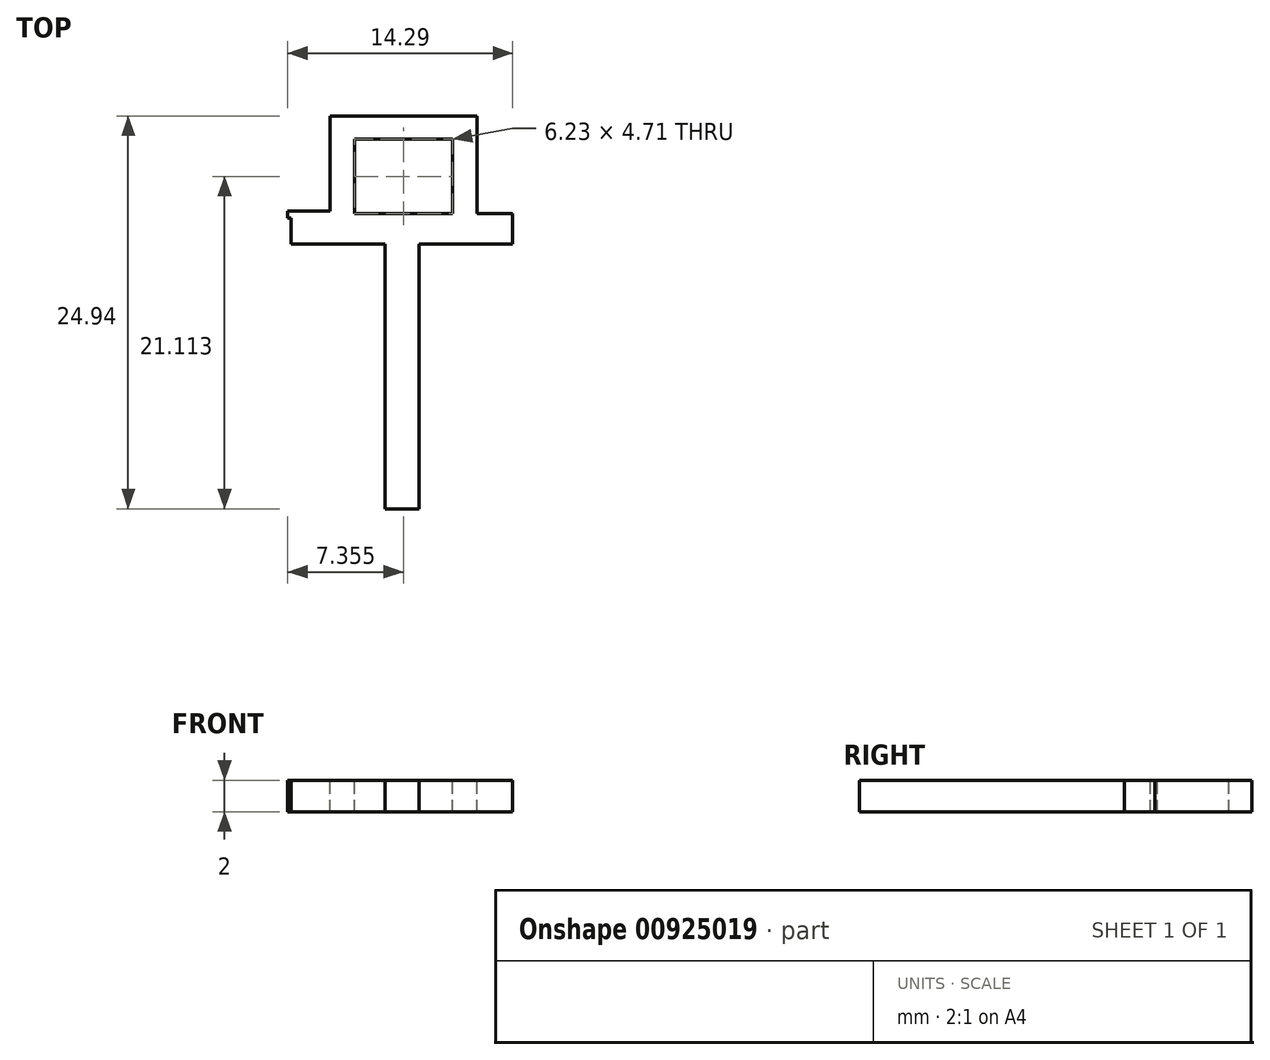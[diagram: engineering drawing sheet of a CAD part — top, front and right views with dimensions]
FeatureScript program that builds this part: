
annotation { "Feature Type Name" : "Feature", "Feature Type Description" : "" }
export const myFeature = defineFeature(function(context is Context, id is Id, definition is map)
    precondition{}
    {
        {
            var Q0;
            Q0=qCreatedBy(makeId("Top.planeOp"),FACE);
            var sketch = newSketch(context, id + "F0", { "sketchPlane" : qUnion([Q0])});
            skText(sketch, "E0", { "text": "T", "fontName": "OpenSans-Regular.ttf"});
            skLineSegment(sketch, "E1", {"start": v(0, 0) * mm, "end": v(16, 0) * mm});
            skLineSegment(sketch, "E2", {"start": v(0, -0.45) * mm, "end": v(0, 0) * mm});
            skLineSegment(sketch, "E3", {"start": v(0, -0.45) * mm, "end": v(16, -0.45) * mm});
            skLineSegment(sketch, "E4", {"start": v(8, -0.45) * mm, "end": v(8, 0) * mm});
            skLineSegment(sketch, "E5.bottom", {"start": v(2.69, -1.92) * mm, "end": v(12.02, -1.92) * mm});
            skLineSegment(sketch, "E5.top", {"start": v(2.69, 6.02) * mm, "end": v(12.02, 6.02) * mm});
            skLineSegment(sketch, "E5.left", {"start": v(2.69, -1.92) * mm, "end": v(2.69, 6.02) * mm});
            skLineSegment(sketch, "E5.right", {"start": v(12.02, -1.92) * mm, "end": v(12.02, 6.02) * mm});
            skLineSegment(sketch, "E6", {"start": v(7.36, 6.02) * mm, "end": v(7.36, -1.92) * mm});
            skLineSegment(sketch, "E7.bottom", {"start": v(10.47, -0.45) * mm, "end": v(4.24, -0.45) * mm});
            skLineSegment(sketch, "E7.top", {"start": v(10.47, 4.55) * mm, "end": v(4.24, 4.55) * mm});
            skLineSegment(sketch, "E7.left", {"start": v(10.47, -0.45) * mm, "end": v(10.47, 4.55) * mm});
            skLineSegment(sketch, "E7.right", {"start": v(4.24, -0.45) * mm, "end": v(4.24, 4.55) * mm});
            skPoint(sketch, "E7.middle", {"position": v(7.36, 2.05) * mm});
            const initialGuessF0  = {"E0": [0, -0.01892, 1, 0, 0.01892]};
            skSetInitialGuess(sketch, initialGuessF0);
            skSolve(sketch);
        }
        {
            var Q0;
            Q0 = qSketchRegion(id + "F0", true);
            var Q1;
            {var subQ0=sQuery(id+"F0.wireOp",EDGE,"E5.right");var subQ1=sQuery(id+"F0.wireOp",EDGE,"E5.bottom");var subQ2=makeQuery(id+"F0.imprint","INTERSECT",VERTEX,{"derivedFrom":[subQ1,subQ0]});Q1=makeQuery(id+"F0.imprint","IMPRINT",FACE,{"disambiguationData":[TD([[makeQuery(id+"F0.imprint","IMPRINT",EDGE,{"disambiguationData":[TD([[subQ2,1.0]])],"derivedFrom":subQ1}),1.0]])]});}
            var Q2;
            {var subQ1=sQuery(id+"F0.wireOp",EDGE,"E5.bottom");var subQ5=sQuery(id+"F0.wireOp",EDGE,"E5.left");var subQ6=makeQuery(id+"F0.imprint","INTERSECT",VERTEX,{"derivedFrom":[subQ1,subQ5]});Q2=makeQuery(id+"F0.imprint","IMPRINT",FACE,{"disambiguationData":[TD([[makeQuery(id+"F0.imprint","IMPRINT",EDGE,{"disambiguationData":[TD([[subQ6,-1.0]])],"derivedFrom":subQ1}),1.0]])]});}
            var Q3;
            {var subQ0=sQuery(id+"F0.wireOp",EDGE,"E5.left");var subQ1=sQuery(id+"F0.wireOp",EDGE,"E0.sketch_text.stroke-4");var subQ2=makeQuery(id+"F0.imprint","INTERSECT",VERTEX,{"derivedFrom":[subQ1,subQ0]});Q3=makeQuery(id+"F0.imprint","IMPRINT",FACE,{"disambiguationData":[TD([[makeQuery(id+"F0.imprint","IMPRINT",EDGE,{"disambiguationData":[TD([[subQ2,-1.0]])],"derivedFrom":subQ1}),-1.0]])]});}
            var Q4;
            {var subQ0=sQuery(id+"F0.wireOp",EDGE,"E7.right");var subQ1=sQuery(id+"F0.wireOp",EDGE,"E0.sketch_text.stroke-4");var subQ2=makeQuery(id+"F0.imprint","INTERSECT",VERTEX,{"derivedFrom":[subQ1,subQ0]});Q4=makeQuery(id+"F0.imprint","IMPRINT",FACE,{"disambiguationData":[TD([[makeQuery(id+"F0.imprint","IMPRINT",EDGE,{"disambiguationData":[TD([[subQ2,-1.0]])],"derivedFrom":subQ1}),-1.0]])]});}
            var Q5;
            {var subQ0=sQuery(id+"F0.wireOp",EDGE,"E4");var subQ1=sQuery(id+"F0.wireOp",EDGE,"E0.sketch_text.stroke-4");var subQ2=makeQuery(id+"F0.imprint","INTERSECT",VERTEX,{"derivedFrom":[subQ1,subQ0]});Q5=makeQuery(id+"F0.imprint","IMPRINT",FACE,{"disambiguationData":[TD([[makeQuery(id+"F0.imprint","IMPRINT",EDGE,{"disambiguationData":[TD([[subQ2,-1.0]])],"derivedFrom":subQ1}),-1.0]])]});}
            var Q6;
            {var subQ0=sQuery(id+"F0.wireOp",EDGE,"E6");var subQ1=sQuery(id+"F0.wireOp",EDGE,"E0.sketch_text.stroke-4");var subQ2=makeQuery(id+"F0.imprint","INTERSECT",VERTEX,{"derivedFrom":[subQ1,subQ0]});Q6=makeQuery(id+"F0.imprint","IMPRINT",FACE,{"disambiguationData":[TD([[makeQuery(id+"F0.imprint","IMPRINT",EDGE,{"disambiguationData":[TD([[subQ2,-1.0]])],"derivedFrom":subQ1}),-1.0]])]});}
            extrude(context, id + "F1", {"entities" : qUnion([Q0, Q1, Q2, Q3, Q4, Q5, Q6]), "oppositeDirection" : true, "depth" : 2 * mm, "offsetDistance" : 25 * mm});
        }
    });
